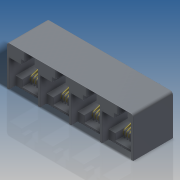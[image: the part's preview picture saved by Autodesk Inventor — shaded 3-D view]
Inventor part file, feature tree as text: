
AUTODESK INVENTOR PART (.ipt)
format: ipt  version: 2016 SP2 (Build 200236200, 236)  size: 648,192 bytes
history: native  units: in
note: dims shown in document units (in); Inventor stores cm internally (conversion verified against a paired STEP export)
features: extrude x7, sketch x4, pattern_linear x3, fillet x2, plane x1, sweep x1
ambient origin geometry x8: Origin, YZ Plane, XZ Plane, XY Plane, X Axis, Y Axis, Z Axis, Center Point
bodies: Solid1 (feature_tree)
feature tree (18):
  sketch  "Sketch2"  dims[d0=1.7953in d1=0.5732in]
  extrude  "Extrusion1"  Depth=0.5732in
  extrude  "Extrusion2"  Depth=0.4094in
  extrude  "Extrusion3"  Depth=0.1417in
  extrude  "Extrusion4"  Depth=0.0787in
  extrude  "Extrusion5"  Depth=0.063in
  extrude  "Extrusion6"  Depth=0.0315in
  sketch  "Sketch3"  dims[d2=0.0378in d3=0.4094in]
  plane  "Work Plane1"
  sweep  "Sweep1"
  pattern_linear  "Rectangular Pattern1"  Spacing1=0.0945in  [1 undecoded]
  extrude  "Extrusion7"  Depth=0.0157in
  fillet  "Fillet1"  Radius=0.2205in
  pattern_linear  "Rectangular Pattern2"  Spacing1=0.5669in  [1 undecoded]
  pattern_linear  "Rectangular Pattern3"  Spacing1=0.5039in  [1 undecoded]
  fillet  "Fillet2"  Radius=0.1102in
  sketch  "Sketch4"  dims[d4=0.0378in d5=0.1417in]
  sketch  "Sketch5"  dims[d6=0.2362in d8=0.0787in d9=0.063in d10=0.0315in d11=0.126in d12=0.0945in d13=0.0157in d14=0.2205in d15=0.5669in d16=0.0in d17=0.5039in d18=0.0in d19=0.1102in d20=0.0in d21=0.378in d22=0.0in d23=0.0945in d24=0.0in d25=0.189in d26=0.0in d27=0.0228in d28=0.0114in d29=0.0394in d31=0.0709in d32=0.0866in d33=0.0in d34=2.3622in d36=0.0394in d37=0.0315in d38=0.1417in d39=0.0in d40=0.0039in d41=1.5748in d43=0.4409in d44=1.5748in d46=0.4409in d47=0.0039in d48=0.0in]
note: 3 required parameter values undecoded (feature->parameter linkage not recoverable at this tier; creation-order binding heuristic only, values carry confidence <= 0.55)
